SOLIDWORKS PART (.sldprt)
format: sldprt  version: not decoded by parser v0  size: 326,144 bytes
history: native  units: mm
features: plane x3, sketch x3, cut_extrude x2, material x1, extrude x1 (+9 scaffold rows collapsed)
feature tree (19):
  scaffold x9  (default folders/planes/origin — collapsed)
  material  "Matériau <non spécifié>"
  plane  "Plane1"
  plane  "Plane2"
  plane  "Plane3"
  sketch  "Esquisse1"  dims[c1.D2=~1.485839mm c1.D1=~3.926991mm c2.D2=5.625mm c2.D3=22.0mm c2.D4=~1.907671mm c3.D4=110.0deg c3.D5=2.5mm c3.D6=~1.963495mm c3.D1=7.0mm c3.D2=4.5mm]
  extrude  "Extrusion1"  Depth=6mm
  sketch  "Esquisse4"  dims[D1=4.1mm]
  cut_extrude  "Enlèv. mat.-Extru.2"  Depth=2.8mm
  sketch  "Esquisse5"  dims[D1=~1.434474mm]
  cut_extrude  "Enlèv. mat.-Extru.3"  Depth=2.5mm
decode coverage: 6 of 6 modeling features carry decoded parameters
note: ~ marks probable driven/reference dimensions
note: suppression state not decoded; provenance and decode notes live in map.json
